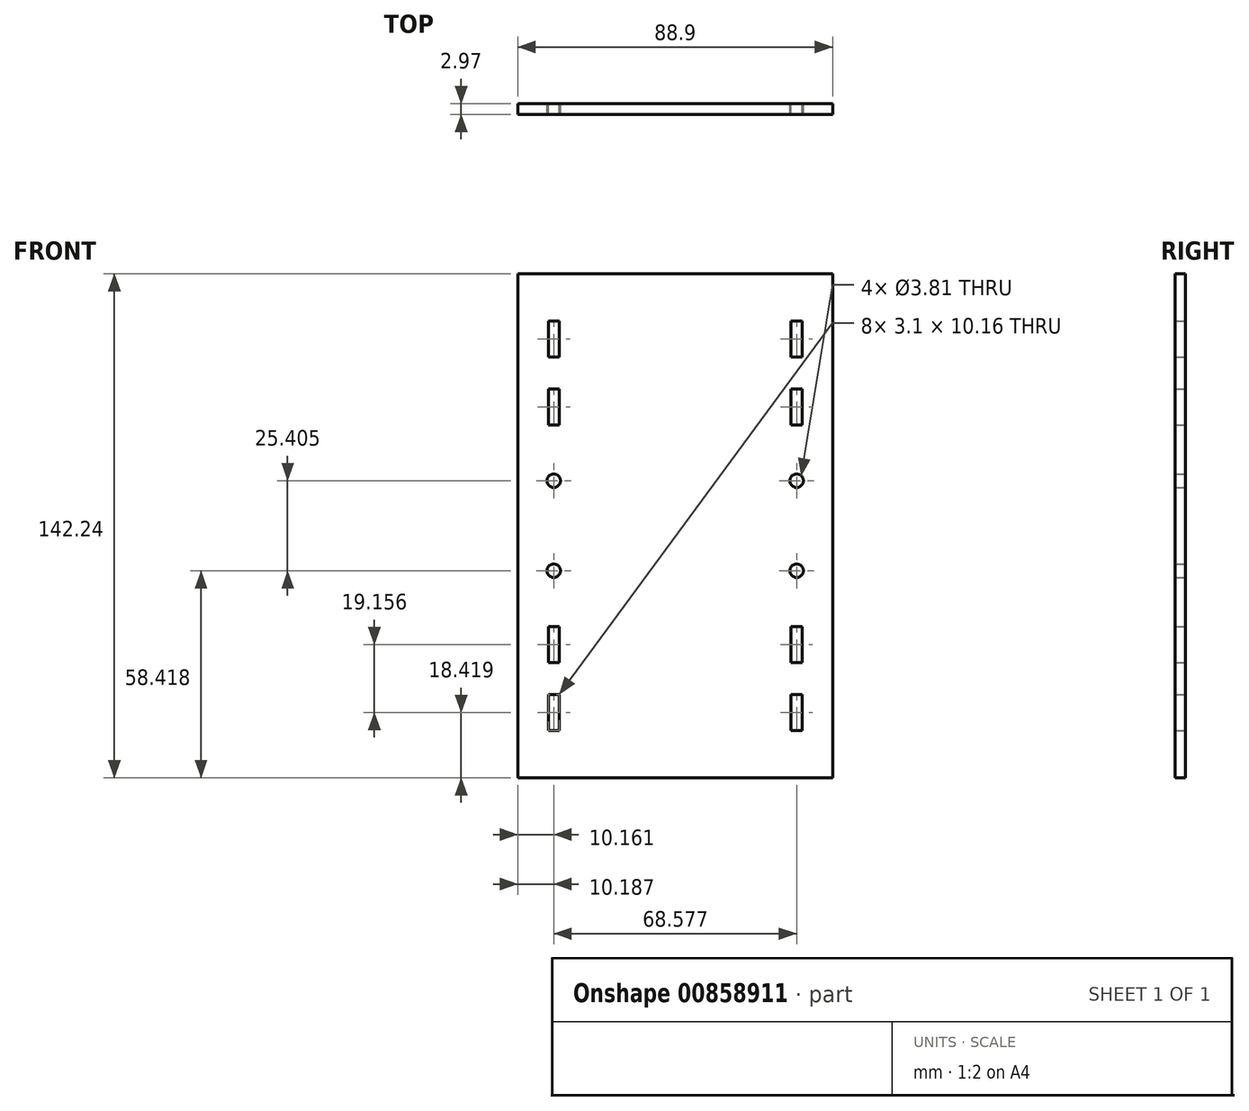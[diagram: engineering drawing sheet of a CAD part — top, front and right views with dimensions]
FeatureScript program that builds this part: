
annotation { "Feature Type Name" : "Feature", "Feature Type Description" : "" }
export const myFeature = defineFeature(function(context is Context, id is Id, definition is map)
    precondition{}
    {
        {
            var Q0;
            Q0=qCreatedBy(makeId("Front.planeOp"),FACE);
            var sketch = newSketch(context, id + "F0", { "sketchPlane" : qUnion([Q0])});
            skLineSegment(sketch, "E0.bottom", {"start": v(-44.45, 71.12) * mm, "end": v(44.45, 71.12) * mm});
            skLineSegment(sketch, "E0.top", {"start": v(-44.45, -71.12) * mm, "end": v(44.45, -71.12) * mm});
            skLineSegment(sketch, "E0.left", {"start": v(-44.45, 71.12) * mm, "end": v(-44.45, -71.12) * mm});
            skLineSegment(sketch, "E0.right", {"start": v(44.45, 71.12) * mm, "end": v(44.45, -71.12) * mm});
            skPoint(sketch, "E0.middle", {"position": v(0, 0) * mm});
            skLineSegment(sketch, "E1.MirrorCS", {"start": v(44.45, 0) * mm, "end": v(40.64, 0) * mm});
            skLineSegment(sketch, "E2", {"start": v(-44.45, 0) * mm, "end": v(-34.29, 0) * mm});
            skLineSegment(sketch, "E3", {"start": v(-34.29, 0) * mm, "end": v(-34.29, 12.7) * mm});
            skSolve(sketch);
        }
        {
            var Q0;
            Q0=qCreatedBy(makeId("Front.planeOp"),FACE);
            var sketch = newSketch(context, id + "F1", { "sketchPlane" : qUnion([Q0])});
            skCircle(sketch, "E4", {"center": v(-34.29, 12.7) * mm, "radius": 1.9 * mm});
            skCircle(sketch, "E5.MirrorC", {"center": v(-34.29, -12.7) * mm, "radius": 1.9 * mm});
            skCircle(sketch, "E6.MirrorC", {"center": v(34.29, 12.7) * mm, "radius": 1.9 * mm});
            skCircle(sketch, "E7.MirrorC", {"center": v(34.29, -12.7) * mm, "radius": 1.9 * mm});
            skLineSegment(sketch, "E8.bottom", {"start": v(-35.81, 57.78) * mm, "end": v(-32.71, 57.78) * mm});
            skLineSegment(sketch, "E8.top", {"start": v(-35.81, 47.62) * mm, "end": v(-32.71, 47.62) * mm});
            skLineSegment(sketch, "E8.left", {"start": v(-35.81, 57.78) * mm, "end": v(-35.81, 47.62) * mm});
            skLineSegment(sketch, "E8.right", {"start": v(-32.71, 57.78) * mm, "end": v(-32.71, 47.62) * mm});
            skLineSegment(sketch, "E9.MirrorCS", {"start": v(-35.81, 28.46) * mm, "end": v(-35.81, 38.62) * mm});
            skLineSegment(sketch, "E10.MirrorCS", {"start": v(-35.81, 28.46) * mm, "end": v(-32.71, 28.46) * mm});
            skLineSegment(sketch, "E11.MirrorCS", {"start": v(-32.71, 28.46) * mm, "end": v(-32.71, 38.62) * mm});
            skLineSegment(sketch, "E12.MirrorCS", {"start": v(-35.81, 38.62) * mm, "end": v(-32.71, 38.62) * mm});
            skLineSegment(sketch, "E13.MirrorCS", {"start": v(-32.71, -28.46) * mm, "end": v(-32.71, -38.62) * mm});
            skLineSegment(sketch, "E14.MirrorCS", {"start": v(-35.81, -28.46) * mm, "end": v(-35.81, -38.62) * mm});
            skLineSegment(sketch, "E15.MirrorCS", {"start": v(-35.81, -28.46) * mm, "end": v(-32.71, -28.46) * mm});
            skLineSegment(sketch, "E16.MirrorCS", {"start": v(-35.81, -38.62) * mm, "end": v(-32.71, -38.62) * mm});
            skLineSegment(sketch, "E17.MirrorCS", {"start": v(-35.81, -47.62) * mm, "end": v(-32.71, -47.62) * mm});
            skLineSegment(sketch, "E18.MirrorCS", {"start": v(-35.81, -57.78) * mm, "end": v(-35.81, -47.62) * mm});
            skLineSegment(sketch, "E19.MirrorCS", {"start": v(-35.81, -57.78) * mm, "end": v(-32.71, -57.78) * mm});
            skLineSegment(sketch, "E20.MirrorCS", {"start": v(-32.71, -57.78) * mm, "end": v(-32.71, -47.62) * mm});
            skLineSegment(sketch, "E21.MirrorCS", {"start": v(32.71, 57.78) * mm, "end": v(32.71, 47.62) * mm});
            skLineSegment(sketch, "E22.MirrorCS", {"start": v(35.81, 57.78) * mm, "end": v(32.71, 57.78) * mm});
            skLineSegment(sketch, "E23.MirrorCS", {"start": v(35.81, 57.78) * mm, "end": v(35.81, 47.62) * mm});
            skLineSegment(sketch, "E24.MirrorCS", {"start": v(35.81, 47.62) * mm, "end": v(32.71, 47.62) * mm});
            skLineSegment(sketch, "E25.MirrorCS", {"start": v(35.81, 38.62) * mm, "end": v(32.71, 38.62) * mm});
            skLineSegment(sketch, "E26.MirrorCS", {"start": v(35.81, 28.46) * mm, "end": v(35.81, 38.62) * mm});
            skLineSegment(sketch, "E27.MirrorCS", {"start": v(35.81, 28.46) * mm, "end": v(32.71, 28.46) * mm});
            skLineSegment(sketch, "E28.MirrorCS", {"start": v(32.71, 28.46) * mm, "end": v(32.71, 38.62) * mm});
            skLineSegment(sketch, "E29.MirrorCS", {"start": v(32.71, -28.46) * mm, "end": v(32.71, -38.62) * mm});
            skLineSegment(sketch, "E30.MirrorCS", {"start": v(35.81, -38.62) * mm, "end": v(32.71, -38.62) * mm});
            skLineSegment(sketch, "E31.MirrorCS", {"start": v(35.81, -28.46) * mm, "end": v(35.81, -38.62) * mm});
            skLineSegment(sketch, "E32.MirrorCS", {"start": v(35.81, -28.46) * mm, "end": v(32.71, -28.46) * mm});
            skLineSegment(sketch, "E33.MirrorCS", {"start": v(32.71, -57.78) * mm, "end": v(32.71, -47.62) * mm});
            skLineSegment(sketch, "E34.MirrorCS", {"start": v(35.81, -47.62) * mm, "end": v(32.71, -47.62) * mm});
            skLineSegment(sketch, "E35.MirrorCS", {"start": v(35.81, -57.78) * mm, "end": v(35.81, -47.62) * mm});
            skLineSegment(sketch, "E36.MirrorCS", {"start": v(35.81, -57.78) * mm, "end": v(32.71, -57.78) * mm});
            skLineSegment(sketch, "E37", {"start": v(0, 0) * mm, "end": v(-32.71, 0) * mm});
            skLineSegment(sketch, "E38", {"start": v(-35.81, 28.46) * mm, "end": v(-35.81, 0) * mm});
            skLineSegment(sketch, "E39", {"start": v(-35.81, 47.62) * mm, "end": v(-35.81, 38.62) * mm});
            skLineSegment(sketch, "E40", {"start": v(-34.29, 12.7) * mm, "end": v(-34.29, 0) * mm});
            skLineSegment(sketch, "E41", {"start": v(-44.52, -71) * mm, "end": v(0, -71) * mm});
            skSolve(sketch);
        }
        {
            var Q0;
            Q0 = qSketchRegion(id + "F0", true);
            extrude(context, id + "F2", {"entities" : qUnion([Q0]), "depth" : 2.97 * mm, "offsetDistance" : 25.4 * mm});
        }
        {
            var Q0;
            Q0 = qSketchRegion(id + "F1", true);
            extrude(context, id + "F3", {"entities" : qUnion([Q0]), "operationType" : NewBodyOperationType.REMOVE, "depth" : 29.72 * mm, "offsetDistance" : 25.4 * mm});
        }
    });
